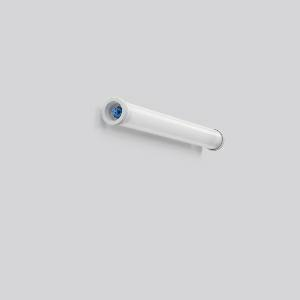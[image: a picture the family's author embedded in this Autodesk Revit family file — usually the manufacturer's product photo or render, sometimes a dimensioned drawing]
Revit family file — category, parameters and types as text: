
# Revit family: planox_tube_601070_002_1_c6ff
name_source: partatom
category: Lighting Fixtures
units: mm (PartAtom-declared; Revit-internal decimal feet)

## family parameters
Cut with Voids When Loaded = No
Host = Face
Light Source = No
Part Type = Normal
Room Calculation Point = No
Round Connector Dimension = Use Diameter
Shared = No

## types (1)
- PLANOX TUBE (1 x LED Modul 840, 3500 lm, 4000)
    Apparent Load = 31 VA
    CIE Flux Codes = 41 70 89 89 100
    Color Rendering = 80
    Color Temperature = 4000
    Default Elevation = 1800 mm
    Description = Series: PLANOX TUBE
Robust protective tube luminaire for tough requirements. Rack made of sheet steel, white powder coated. End caps made of plastic (polyamide) grey. Diffuser made of plastic (polycarbonate), opal, shockproof. Symmetrical light distribution. Homogeneous light distribution. With accessories for wall, ceiling or pendant mounting. Driver integrated. Easy installation with the Plug+Play Wieland RST CLASSIC plug-in system. Luminaire with integrated through-wiring for series connection of further luminaires by two Wieland RST Classic plug connectors (plug and socket). Accessories for electrical connection must be ordered separately. Mounting set must be ordered separately. Luminaire with limited surface temperature in accordance with EN 60598-2-24 for use in environments in which a deposit of conductive dust on the luminaire can be expected. Qualified for use in the food and drink industry. Suitable for lighting in public car parks and public off-street parking spaces according to DIN 67528. Environmentally friendly and resource-saving due to replaceable components. 
Colour: white
Diameter: 78 mm
Length: 722 mm
Lamp: LED
Socket: without socket
Colour temperature: 4000K
Colour rendering index (CRI): 83
System power: 31 W
Rated luminous flux: 3500 lm
Luminous efficiency: 113 lm/W
Control gear: Regulated power supply
Protection class: I
Type of protection: IP 67
    Height = 0 mm  [stored 0 ft]
    Lamp = 1 x LED Modul 840
    Lamp Light Flux = 3500 lm
    Lamp count = 1
    Length = 722 mm
    Lifetime = 50000 h
    Luminous efficacy = 113 lm/W
    Manufacturer = RZB
    ModVariant = No
    Model = 601070.002.1
    Mounting Place = Ceiling
    Mounting Type = Surface mounted
    Number of Poles = 1
    OnlyDefault = Yes
    Power Factor = 1
    Product Name = PLANOX TUBE
    Product group = Surface mounted luminaires for moist/humid enviroments
    ProductGroupID = 308
    Protection Class = Protection class I
    Protection Degree = Degree of protection
    RLX_Detail_Level = 1
    RLX_Emergency_Light_Flux = 0 lm
    RLX_Emergency_Type = 0
    RLX_Emergency_Type_DB = No
    RlxData = <blob elided: 31801 chars, md5=cb9592ac>
    Socket = socket
    Standby Power = 0 W
    System Light Flux = 3500 lm
    System Power = 31 W
    Type Comments = Product without accessories
    Type Image = 601070.002.jpg
    URL = http://relux.com
    VarID = ---
    Voltage = 0 V
    Weight = 0.00 kg
    Width = 0 mm  [stored 0 ft]

note: [stored X ft] marks values corroborated as IEEE doubles in the binary element streams (Revit-internal decimal feet)

## geometry (parser evidence)
native form markers: Blend x4, Sweep x14
no freeform markers — native parametric forms only
